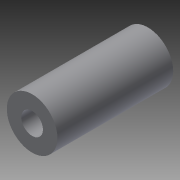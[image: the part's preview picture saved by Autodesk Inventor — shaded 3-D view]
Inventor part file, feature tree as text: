
AUTODESK INVENTOR PART (.ipt)
format: ipt  version: 2015 SP2 (Build 190223200, 223)  size: 82,944 bytes
history: native  units: in
note: dims shown in document units (in); Inventor stores cm internally (conversion verified against a paired STEP export)
features: extrude x1, other x1
ambient origin geometry x8: Origin, YZ Plane, XZ Plane, XY Plane, X Axis, Y Axis, Z Axis, Center Point
bodies: Solid1 (feature_tree)
feature tree (2):
  extrude  "profile_extrusion"  Depth=0.3in
  other  "profile_sketch"
